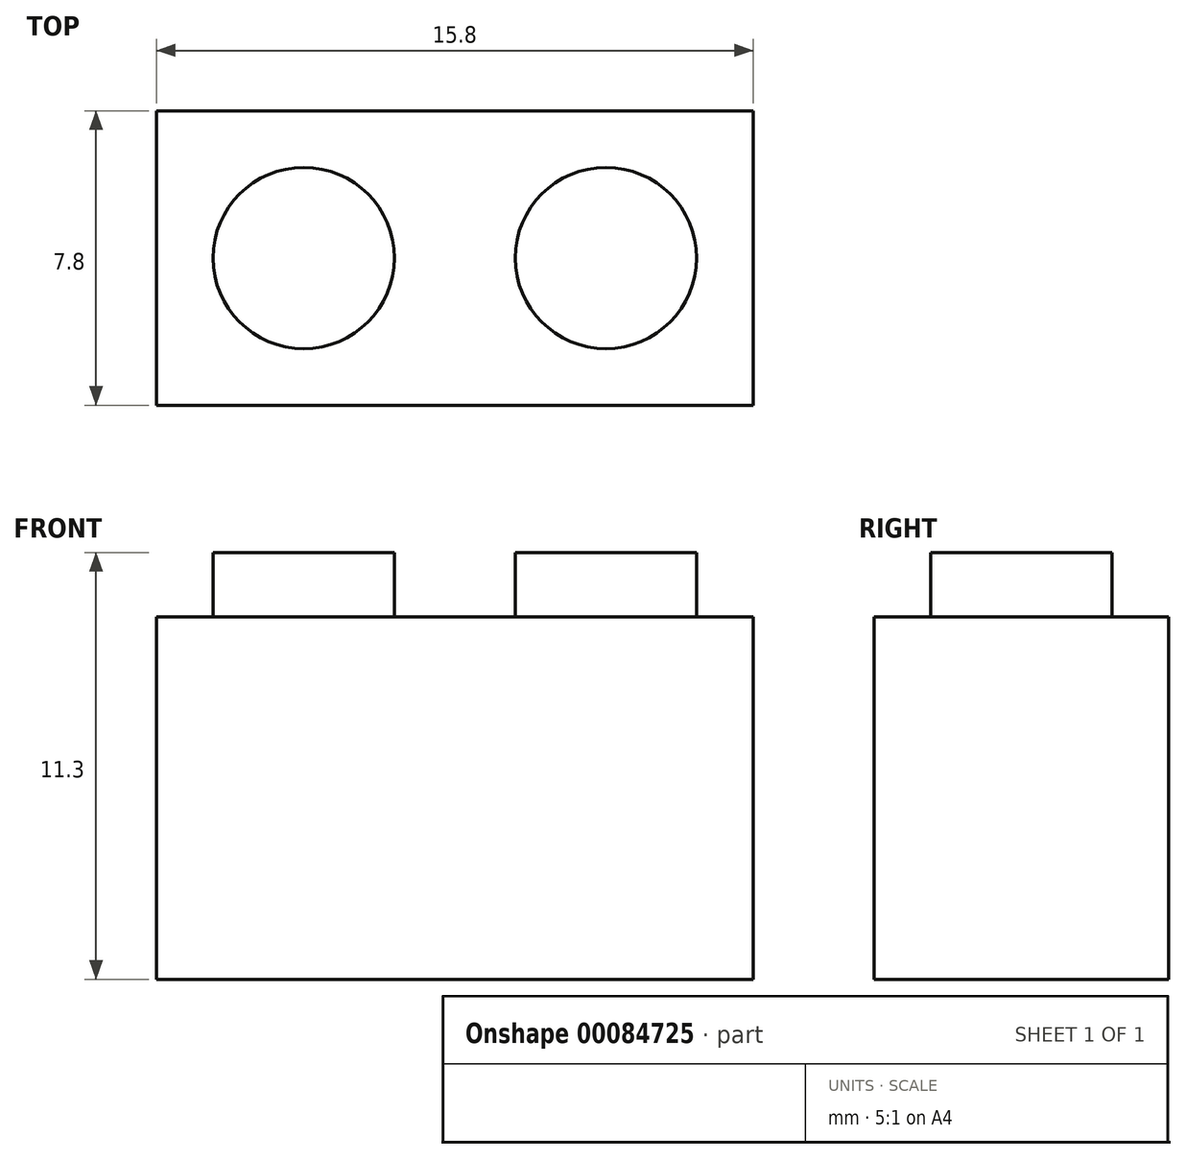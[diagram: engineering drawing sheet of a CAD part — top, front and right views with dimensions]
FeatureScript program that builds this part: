
annotation { "Feature Type Name" : "Feature", "Feature Type Description" : "" }
export const myFeature = defineFeature(function(context is Context, id is Id, definition is map)
    precondition{}
    {
        {
            var Q0;
            Q0=qCreatedBy(makeId("Top.planeOp"),FACE);
            var sketch = newSketch(context, id + "F0", { "sketchPlane" : qUnion([Q0])});
            skLineSegment(sketch, "E0.bottom", {"start": v(-7.9, 3.9) * mm, "end": v(7.9, 3.9) * mm});
            skLineSegment(sketch, "E0.top", {"start": v(-7.9, -3.9) * mm, "end": v(7.9, -3.9) * mm});
            skLineSegment(sketch, "E0.left", {"start": v(-7.9, 3.9) * mm, "end": v(-7.9, -3.9) * mm});
            skLineSegment(sketch, "E0.right", {"start": v(7.9, 3.9) * mm, "end": v(7.9, -3.9) * mm});
            skLineSegment(sketch, "E1", {"start": v(-7.9, 0) * mm, "end": v(7.9, 0) * mm, "construction": true});
            skLineSegment(sketch, "E2", {"start": v(0, -3.9) * mm, "end": v(0, 0) * mm, "construction": true});
            skLineSegment(sketch, "E3", {"start": v(0, 0) * mm, "end": v(0, 3.9) * mm, "construction": true});
            skSolve(sketch);
        }
        {
            var Q0;
            Q0 = qSketchRegion(id + "F0", true);
            extrude(context, id + "F1", {"entities" : qUnion([Q0]), "depth" : 9.6 * mm});
        }
        {
            var Q0;
            Q0=makeQuery(id+"F1.opExtrude","CAP_FACE",FACE,{"disambiguationData":[OSD([sQuery(id+"F0.wireOp",EDGE,"E0.bottom"),sQuery(id+"F0.wireOp",EDGE,"E0.top"),sQuery(id+"F0.wireOp",EDGE,"E0.left"),sQuery(id+"F0.wireOp",EDGE,"E0.right")])],"isStart":false});
            var sketch = newSketch(context, id + "F2", { "sketchPlane" : qUnion([Q0])});
            skCircle(sketch, "E4", {"center": v(4, 0) * mm, "radius": 2.4 * mm});
            skLineSegment(sketch, "E5.bottom", {"start": v(4, 0) * mm, "end": v(-4, 0) * mm, "construction": true});
            skCircle(sketch, "E6", {"center": v(-4, 0) * mm, "radius": 2.4 * mm});
            skSolve(sketch);
        }
        {
            var Q0;
            Q0 = qSketchRegion(id + "F2", true);
            extrude(context, id + "F3", {"entities" : qUnion([Q0]), "operationType" : NewBodyOperationType.ADD, "depth" : 1.7 * mm});
        }
    });
